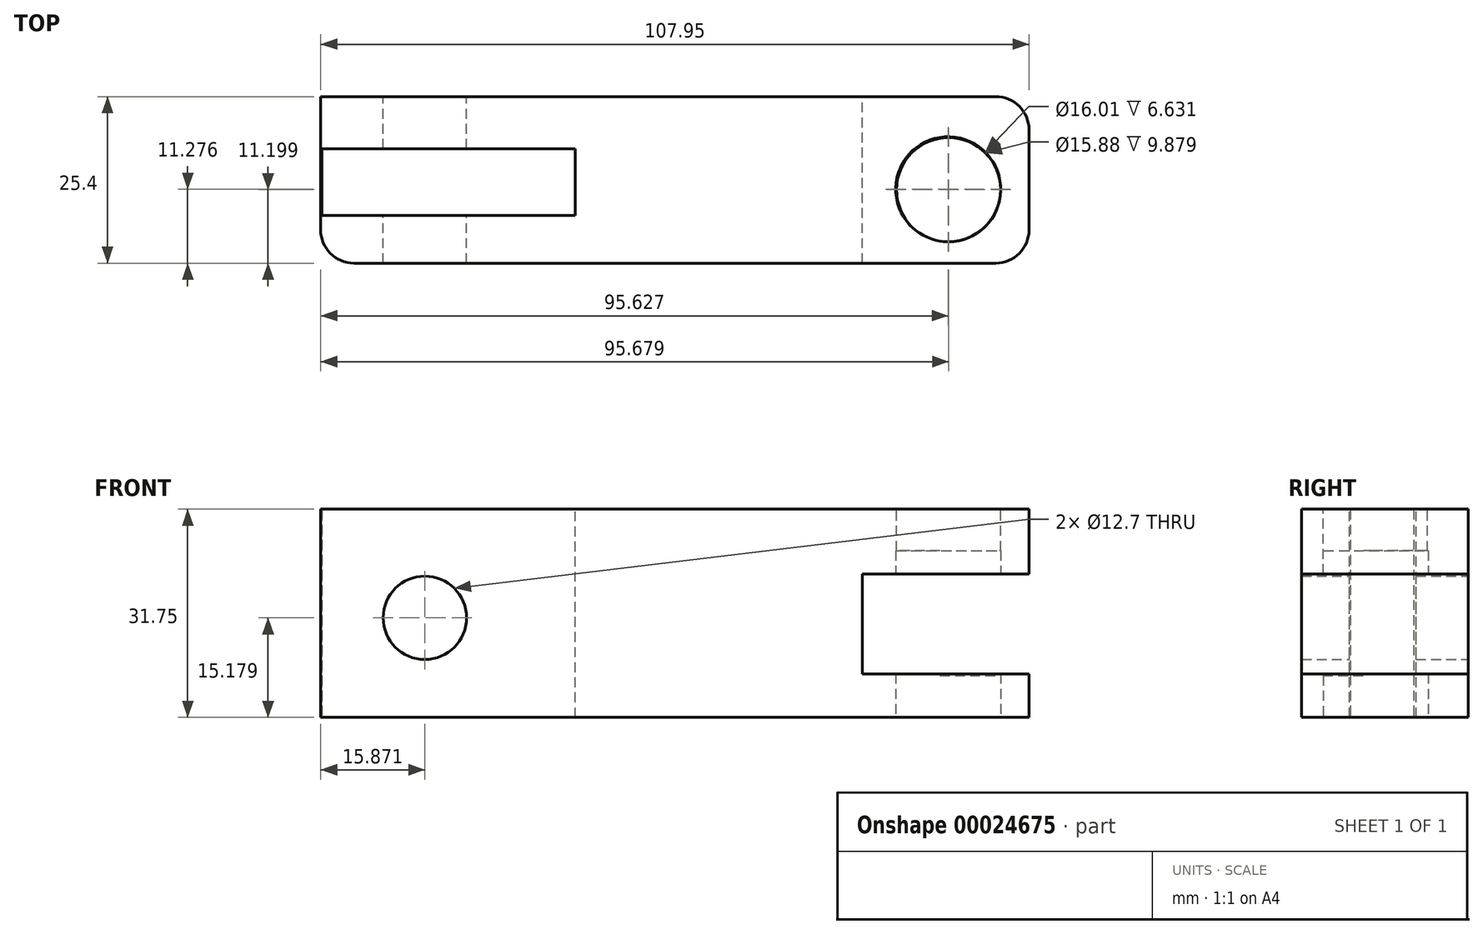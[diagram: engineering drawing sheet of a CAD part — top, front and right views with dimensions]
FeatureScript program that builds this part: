
annotation { "Feature Type Name" : "Feature", "Feature Type Description" : "" }
export const myFeature = defineFeature(function(context is Context, id is Id, definition is map)
    precondition{}
    {
        {
            var Q0;
            Q0=qCreatedBy(makeId("Front.planeOp"),FACE);
            var sketch = newSketch(context, id + "F0", { "sketchPlane" : qUnion([Q0])});
            skLineSegment(sketch, "E0.bottom", {"start": v(-62.9, 14.15) * mm, "end": v(45.06, 14.15) * mm});
            skLineSegment(sketch, "E0.top", {"start": v(-62.9, -17.6) * mm, "end": v(45.06, -17.6) * mm});
            skLineSegment(sketch, "E0.left", {"start": v(-62.9, 14.15) * mm, "end": v(-62.9, -17.6) * mm});
            skLineSegment(sketch, "E0.right", {"start": v(45.06, 14.15) * mm, "end": v(45.06, -17.6) * mm});
            skLineSegment(sketch, "E1.0", {"start": v(-47.02, 14.15) * mm, "end": v(-47.02, 13.31) * mm, "construction": true});
            skArc(sketch, "E2", {"start": v(-47.02, 13.31) * mm, "mid": v(-62.61, -4.51) * mm, "end": v(-42.87, -17.6) * mm});
            skCircle(sketch, "E3", {"center": v(-47.02, -2.42) * mm, "radius": 6.35 * mm});
            skSolve(sketch);
        }
        {
            var Q0;
            {var subQ0=sQuery(id+"F0.wireOp",EDGE,"E2");var subQ1=sQuery(id+"F0.wireOp",EDGE,"E0.top");var subQ3=makeQuery(id+"F0.imprint","INTERSECT",VERTEX,{"disambiguationData":[OD(0.0)],"derivedFrom":[subQ1,subQ0]});Q0=makeQuery(id+"F0.imprint","IMPRINT",FACE,{"disambiguationData":[TD([[makeQuery(id+"F0.imprint","IMPRINT",EDGE,{"disambiguationData":[TD([[subQ3,1.0]])],"derivedFrom":subQ1}),-1.0]])]});}
            var Q1;
            Q1=makeQuery(id+"F0.imprint","IMPRINT",FACE,{"disambiguationData":[TD([[makeQuery(id+"F0.imprint","IMPRINT",EDGE,{"derivedFrom":sQuery(id+"F0.wireOp",EDGE,"E0.bottom")}),-1.0]])]});
            extrude(context, id + "F1", {"entities" : qUnion([Q0, Q1]), "depth" : 25.4 * mm});
        }
        {
            var Q0;
            Q0=makeQuery(id+"F1.opExtrude","CAP_FACE",FACE,{"disambiguationData":[OSD([sQuery(id+"F0.wireOp",EDGE,"E0.bottom"),sQuery(id+"F0.wireOp",EDGE,"E0.top"),sQuery(id+"F0.wireOp",EDGE,"E0.left"),sQuery(id+"F0.wireOp",EDGE,"E0.right"),sQuery(id+"F0.wireOp",EDGE,"E2"),sQuery(id+"F0.wireOp",EDGE,"E3")])],"isStart":false});
            var sketch = newSketch(context, id + "F2", { "sketchPlane" : qUnion([Q0])});
            skSolve(sketch);
        }
        {
            var Q0;
            Q0=makeQuery(id+"F1.opExtrude","SWEPT_FACE",FACE,{"disambiguationData":[OSD([sQuery(id+"F0.wireOp",EDGE,"E0.bottom")])]});
            var sketch = newSketch(context, id + "F3", { "sketchPlane" : qUnion([Q0])});
            skCircle(sketch, "E4", {"center": v(32.79, -14.2) * mm, "radius": 7.94 * mm});
            skSolve(sketch);
        }
        {
            var Q0;
            Q0=makeQuery(id+"F3.imprint","IMPRINT",FACE,{"disambiguationData":[TD([[makeQuery(id+"F3.imprint","IMPRINT",EDGE,{"derivedFrom":sQuery(id+"F3.wireOp",EDGE,"E4")}),-1.0]])]});
            var sketch = newSketch(context, id + "F4", { "sketchPlane" : qUnion([Q0])});
            skLineSegment(sketch, "E5.bottom", {"start": v(-62.7, -7.97) * mm, "end": v(-24.13, -7.97) * mm});
            skLineSegment(sketch, "E5.top", {"start": v(-62.7, -18.13) * mm, "end": v(-24.13, -18.13) * mm});
            skLineSegment(sketch, "E5.left", {"start": v(-62.7, -7.97) * mm, "end": v(-62.7, -18.13) * mm});
            skLineSegment(sketch, "E5.right", {"start": v(-24.13, -7.97) * mm, "end": v(-24.13, -18.13) * mm});
            skSolve(sketch);
        }
        {
            var Q0;
            Q0 = qSketchRegion(id + "F4", true);
            extrude(context, id + "F5", {"entities" : qUnion([Q0]), "operationType" : NewBodyOperationType.REMOVE, "oppositeDirection" : true, "depth" : 25.4 * mm});
        }
        {
            var Q0;
            Q0=makeQuery(id+"F3.imprint","IMPRINT",FACE,{"disambiguationData":[TD([[makeQuery(id+"F3.imprint","IMPRINT",EDGE,{"derivedFrom":sQuery(id+"F3.wireOp",EDGE,"E4")}),1.0]])]});
            var sketch = newSketch(context, id + "F6", { "sketchPlane" : qUnion([Q0])});
            skSolve(sketch);
        }
        {
            var Q0;
            Q0=makeQuery(id+"F1.opExtrude","SWEPT_FACE",FACE,{"disambiguationData":[OSD([sQuery(id+"F0.wireOp",EDGE,"E0.left")])]});
            var sketch = newSketch(context, id + "F7", { "sketchPlane" : qUnion([Q0])});
            skSolve(sketch);
        }
        {
            var Q0;
            {var subQ0=sQuery(id+"F0.wireOp",EDGE,"E0.left");Q0=makeQuery(id+"F7.imprint","IMPRINT",FACE,{"disambiguationData":[TD([[makeQuery(id+"F7.imprint","IMPRINT",EDGE,{"derivedFrom":makeQuery(id+"F1.opExtrude","CAP_EDGE",EDGE,{"disambiguationData":[OSD([subQ0])],"isStart":true})}),1.0]])]});}
            var sketch = newSketch(context, id + "F8", { "sketchPlane" : qUnion([Q0])});
            skLineSegment(sketch, "E6.bottom", {"start": v(8.31, 14.07) * mm, "end": v(18.01, 14.07) * mm});
            skLineSegment(sketch, "E6.top", {"start": v(8.31, -17.28) * mm, "end": v(18.01, -17.28) * mm});
            skLineSegment(sketch, "E6.left", {"start": v(8.31, 14.07) * mm, "end": v(8.31, -17.28) * mm});
            skLineSegment(sketch, "E6.right", {"start": v(18.01, 14.07) * mm, "end": v(18.01, -17.28) * mm});
            skSolve(sketch);
        }
        {
            var Q0;
            Q0 = qSketchRegion(id + "F8", true);
            extrude(context, id + "F9", {"entities" : qUnion([Q0]), "operationType" : NewBodyOperationType.REMOVE, "oppositeDirection" : true, "depth" : 25.4 * mm});
        }
        {
            var Q0;
            Q0=makeQuery(id+"F1.opExtrude","SWEPT_FACE",FACE,{"disambiguationData":[OSD([sQuery(id+"F0.wireOp",EDGE,"E0.right")])]});
            var sketch = newSketch(context, id + "F10", { "sketchPlane" : qUnion([Q0])});
            skLineSegment(sketch, "E7.bottom", {"start": v(-25.4, 4.27) * mm, "end": v(0, 4.27) * mm});
            skLineSegment(sketch, "E7.top", {"start": v(-25.4, -10.97) * mm, "end": v(0, -10.97) * mm});
            skLineSegment(sketch, "E7.left", {"start": v(-25.4, 4.27) * mm, "end": v(-25.4, -10.97) * mm});
            skLineSegment(sketch, "E7.right", {"start": v(0, 4.27) * mm, "end": v(0, -10.97) * mm});
            skSolve(sketch);
        }
        {
            var Q0;
            Q0 = qSketchRegion(id + "F10", true);
            extrude(context, id + "F11", {"entities" : qUnion([Q0]), "operationType" : NewBodyOperationType.REMOVE, "oppositeDirection" : true, "depth" : 25.4 * mm});
        }
        {
            var Q0;
            {var subQ0=sQuery(id+"F0.wireOp",EDGE,"E0.top");Q0=makeQuery(id+"F1.opExtrude","SWEPT_FACE",FACE,{"disambiguationData":[OSD([subQ0]),TDD([makeQuery(id+"F0.imprint","IMPRINT",EDGE,{"disambiguationData":[TD([[makeQuery(id+"F0.imprint","INTERSECT",VERTEX,{"derivedFrom":[subQ0,sQuery(id+"F0.wireOp",EDGE,"E0.right")]}),1.0]])],"derivedFrom":subQ0})])]});}
            var sketch = newSketch(context, id + "F12", { "sketchPlane" : qUnion([Q0])});
            skCircle(sketch, "E8", {"center": v(32.74, 14.12) * mm, "radius": 8 * mm});
            skSolve(sketch);
        }
        {
            var Q0;
            Q0=makeQuery(id+"F12.imprint","IMPRINT",FACE,{"disambiguationData":[TD([[makeQuery(id+"F12.imprint","IMPRINT",EDGE,{"derivedFrom":sQuery(id+"F12.wireOp",EDGE,"E8")}),1.0]])]});
            extrude(context, id + "F13", {"entities" : qUnion([Q0]), "operationType" : NewBodyOperationType.REMOVE, "oppositeDirection" : true, "depth" : 25.4 * mm});
        }
        {
            var Q0;
            Q0=makeQuery(id+"F3.imprint","IMPRINT",FACE,{"disambiguationData":[TD([[makeQuery(id+"F3.imprint","IMPRINT",EDGE,{"derivedFrom":sQuery(id+"F3.wireOp",EDGE,"E4")}),1.0]])]});
            extrude(context, id + "F14", {"entities" : qUnion([Q0]), "operationType" : NewBodyOperationType.REMOVE, "oppositeDirection" : true, "depth" : 25.4 * mm});
        }
        {
            var Q0;
            {var subQ0=sQuery(id+"F0.wireOp",EDGE,"E0.right");var subQ1=sQuery(id+"F0.wireOp",EDGE,"E0.bottom");Q0=makeQuery(id+"F11.boolean.opBoolean","SPLIT",EDGE,{"disambiguationData":[TD([makeQuery(id+"F1.opExtrude","SWEPT_FACE",FACE,{"disambiguationData":[OSD([subQ1])]})])],"derivedFrom":makeQuery(id+"F1.opExtrude","CAP_EDGE",EDGE,{"disambiguationData":[OSD([subQ0])],"isStart":false})});}
            fillet(context, id + "F15", {"entities" : qUnion([Q0]), "radius" : 5.08 * mm, "tangentPropagation" : true, "allowEdgeOverflow" : false});
        }
        {
            var Q0;
            {var subQ0=sQuery(id+"F0.wireOp",EDGE,"E0.right");Q0=makeQuery(id+"F11.boolean.opBoolean","SPLIT",EDGE,{"disambiguationData":[TD([makeQuery(id+"F11.opExtrude","SWEPT_FACE",FACE,{"disambiguationData":[OSD([sQuery(id+"F10.wireOp",EDGE,"E7.top")])]})])],"derivedFrom":makeQuery(id+"F1.opExtrude","CAP_EDGE",EDGE,{"disambiguationData":[OSD([subQ0])],"isStart":false})});}
            fillet(context, id + "F16", {"entities" : qUnion([Q0]), "radius" : 5.08 * mm, "tangentPropagation" : true, "allowEdgeOverflow" : false});
        }
        {
            var Q0;
            {var subQ0=sQuery(id+"F0.wireOp",EDGE,"E0.right");var subQ1=sQuery(id+"F0.wireOp",EDGE,"E0.bottom");Q0=makeQuery(id+"F11.boolean.opBoolean","SPLIT",EDGE,{"disambiguationData":[TD([makeQuery(id+"F1.opExtrude","SWEPT_FACE",FACE,{"disambiguationData":[OSD([subQ1])]})])],"derivedFrom":makeQuery(id+"F1.opExtrude","CAP_EDGE",EDGE,{"disambiguationData":[OSD([subQ0])],"isStart":true})});}
            fillet(context, id + "F17", {"entities" : qUnion([Q0]), "radius" : 5.08 * mm, "tangentPropagation" : true, "allowEdgeOverflow" : false});
        }
        {
            var Q0;
            {var subQ0=sQuery(id+"F0.wireOp",EDGE,"E0.right");Q0=makeQuery(id+"F11.boolean.opBoolean","SPLIT",EDGE,{"disambiguationData":[TD([makeQuery(id+"F11.opExtrude","SWEPT_FACE",FACE,{"disambiguationData":[OSD([sQuery(id+"F10.wireOp",EDGE,"E7.top")])]})])],"derivedFrom":makeQuery(id+"F1.opExtrude","CAP_EDGE",EDGE,{"disambiguationData":[OSD([subQ0])],"isStart":true})});}
            fillet(context, id + "F18", {"entities" : qUnion([Q0]), "radius" : 5.08 * mm, "tangentPropagation" : true, "allowEdgeOverflow" : false});
        }
        {
            var Q0;
            Q0=makeQuery(id+"F1.opExtrude","CAP_EDGE",EDGE,{"disambiguationData":[OSD([sQuery(id+"F0.wireOp",EDGE,"E0.left")])],"isStart":false});
            fillet(context, id + "F19", {"entities" : qUnion([Q0]), "radius" : 5.08 * mm, "tangentPropagation" : true, "allowEdgeOverflow" : false});
        }
        {
            var Q0;
            Q0=makeQuery(id+"F5.boolean.opBoolean","COPY",FACE,{"derivedFrom":makeQuery(id+"F5.opExtrude","CAP_FACE",FACE,{"disambiguationData":[OSD([sQuery(id+"F4.wireOp",EDGE,"E5.bottom"),sQuery(id+"F4.wireOp",EDGE,"E5.top"),sQuery(id+"F4.wireOp",EDGE,"E5.left"),sQuery(id+"F4.wireOp",EDGE,"E5.right")])],"isStart":false})});
            extrude(context, id + "F20", {"entities" : qUnion([Q0]), "operationType" : NewBodyOperationType.REMOVE, "oppositeDirection" : true, "depth" : 25.4 * mm});
        }
        {
            var Q0;
            Q0=makeQuery(id+"F9.boolean.opBoolean","COPY",FACE,{"derivedFrom":makeQuery(id+"F9.opExtrude","SWEPT_FACE",FACE,{"disambiguationData":[OSD([sQuery(id+"F8.wireOp",EDGE,"E6.top")])]})});
            extrude(context, id + "F21", {"entities" : qUnion([Q0]), "operationType" : NewBodyOperationType.REMOVE, "oppositeDirection" : true, "depth" : 25.4 * mm});
        }
    });
